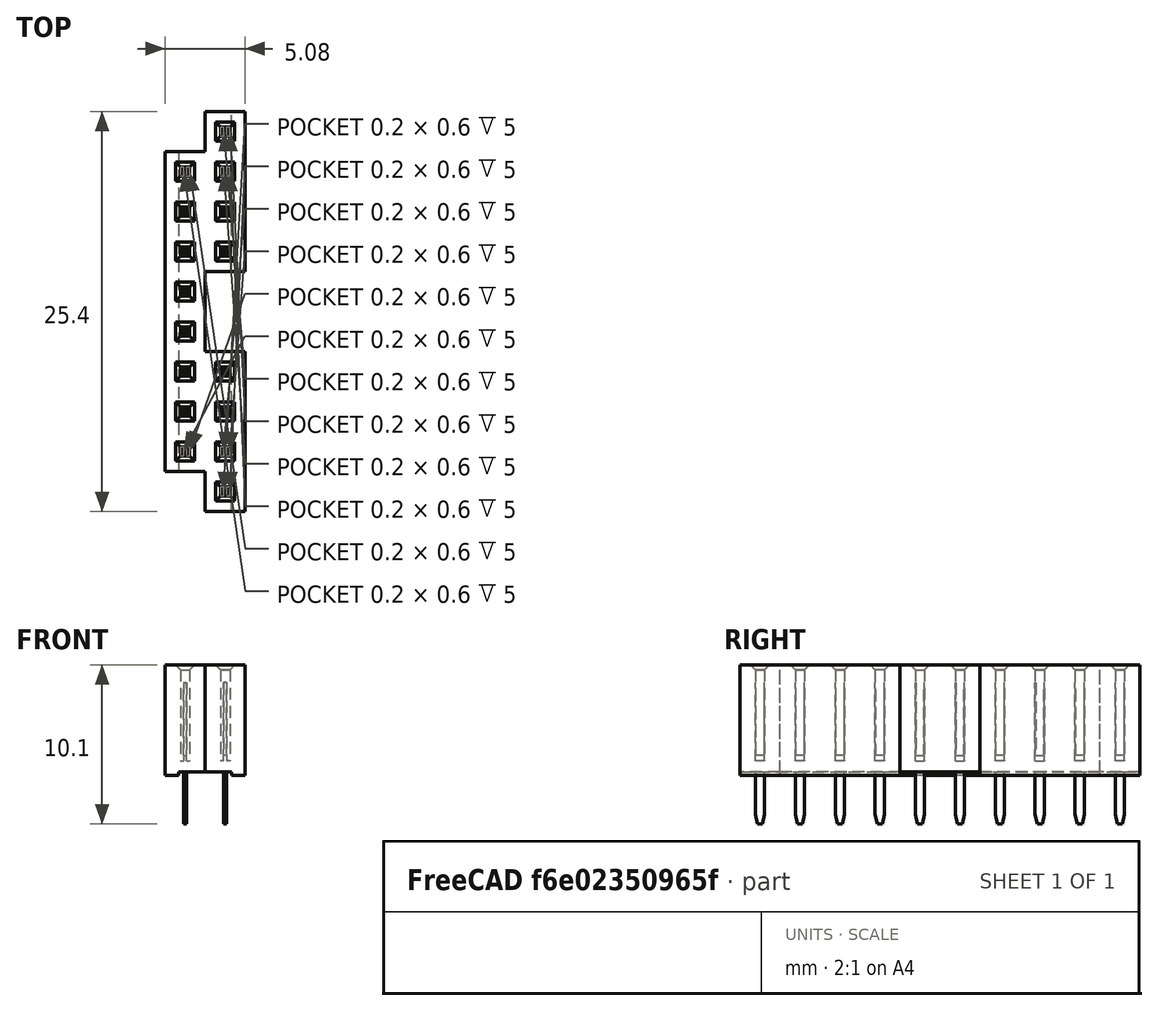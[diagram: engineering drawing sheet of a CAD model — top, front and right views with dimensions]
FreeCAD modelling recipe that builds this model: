
FCSTD DOCUMENT  (FreeCAD 0.18R16146 (Git))
Label: ce-header-connector
License: All rights reserved
LicenseURL: http://en.wikipedia.org/wiki/All_rights_reserved
objects: Part::Box×3, Part::Cut×3, Part::Feature×1
note: 7 computed .brp shape members not serialized (recipe doc carries the construction recipe); baked Part::Feature solids carry a one-line shape summary decoded from their .brp

FEATURE [Part::Feature] Part__Feature  label="PinSocket_2x10_P254mm_Vertical"
  shape: bbox 5.08 x 25.4 x 10.1 mm, 630 faces (baked)
FEATURE [Part::Box] Box  label="Cube"
  AttacherType = Attacher::AttachEngine3D
  Height = 20
  Length = 2.54
  Placement = pos=(-3.81,-1.27,-8) rot=(0,0,1;0rad)
  Width = 2.54
FEATURE [Part::Cut] Cut
  Base = -> Part__Feature
  Tool = -> Box
FEATURE [Part::Box] Box001  label="Cube001"
  AttacherType = Attacher::AttachEngine3D
  Height = 20
  Length = 2.54
  Placement = pos=(-3.81,-24.13,-8) rot=(0,0,1;0rad)
  Width = 2.54
FEATURE [Part::Box] Box002  label="Cube002"
  AttacherType = Attacher::AttachEngine3D
  Height = 20
  Length = 2.54
  Placement = pos=(-1.27,-13.97,-8) rot=(0,0,1;0rad)
  Width = 5.08
FEATURE [Part::Cut] Cut001
  Base = -> Cut
  Tool = -> Box001
FEATURE [Part::Cut] Cut002
  Base = -> Cut001
  Tool = -> Box002
